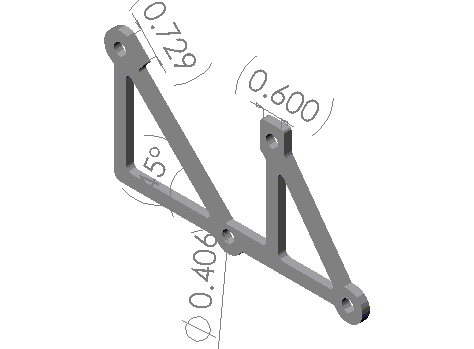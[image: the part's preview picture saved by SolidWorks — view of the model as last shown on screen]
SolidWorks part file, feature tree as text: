
SOLIDWORKS PART (.sldprt)
format: sldprt  version: not decoded by parser v0  size: 442,368 bytes
history: native  units: mm
features: fillet x13, sketch x1, extrude x1 + 1 further entry (+9 scaffold rows collapsed)
feature tree (25):
  "Annotations"  RD1=15.24mm RD2=18.524007mm RD3=45deg RD4=10.3124mm
  scaffold x9  (default folders/planes/origin — collapsed)
  sketch  "Sketch1"  dims[c1.D7=10.3124mm c1.D8=10.3124mm c1.D9=10.3124mm c1.D10=10.3124mm c2.D7=10.3124mm c2.D20=10.3124mm c2.D23=2.54mm c2.D24=2.54mm c2.D25=~12.525847mm c2.D26=~12.460463mm c2.D27=2.54mm c2.D29=7.62mm c2.D30=7.62mm c2.D18=1.27mm c2.D19=2.54mm c2.D31=2.54mm c2.D33=7.62mm c2.D34=1.27mm c2.D35=2.54mm c2.D36=5.08mm c2.D37=2.54mm c2.D38=5.08mm c2.D39=5.08mm c2.D41=7.62mm c2.D14=5.08mm c3.D18=5.08mm c3.D28=5.08mm c3.D30=12.7mm c3.D14=~20.965171mm c4.D28=1.27mm c4.D30=~20.965171mm c4.D18=~13.72589mm c4.D36=10.3124mm c4.D37=10.3124mm c4.D38=10.3124mm c4.D1=25.4mm c4.D2=25.4mm c5.D1=~161.640727mm c6.D1=45.0deg c6.D2=92.075mm c6.D3=~120.52549mm c7.D3=45.0deg c8.D3=92.075mm c8.D4=101.6mm c8.D5=88.9mm c8.D6=~129.320274mm c8.D11=~77.981048mm c9.D11=0.25deg c9.D12=6.35mm c10.D11=~66.14445mm c11.D11=0.0deg c12.D11=6.35mm c12.D12=6.35mm c12.D13=~97.355318mm c13.D13=0.0deg c14.D13=6.35mm c14.D7=6.35mm c14.D9=6.35mm c14.D10=~87.51096mm c15.D10=360.0deg c15.D11=~6.175636mm c16.D10=~86.469108mm c16.D11=~6.175636mm c17.D10=6.35mm c17.D7=6.35mm c17.D9=6.35mm c18.D7=~117.088215mm c19.D7=0.0deg c20.D7=~86.116229mm c21.D7=0.0deg c22.D7=~86.116229mm c23.D7=~0.694885deg c24.D7=~117.088215mm c25.D7=~179.305115deg c26.D7=~117.088215mm c27.D7=0.0deg c28.D7=~130.213714mm c29.D7=0.0deg c30.D7=~64.192579mm c30.D9=~10.081737mm c31.D7=~24.215615mm c32.D7=360.0deg c32.D9=~9.68459mm c33.D7=6.35mm c33.D9=6.35mm c33.D10=6.35mm c33.D11=~89.435083mm c34.D11=0.0deg c35.D11=6.35mm c35.D7=6.35mm c35.D9=~106.448465mm c36.D9=0.0deg c36.D1=~75.270431mm c37.D1=45.0deg c37.D7=~98.145696mm c38.D7=45.0deg c38.D1=~130.213714mm c39.D1=45.0deg c39.D7=6.35mm c39.D9=6.35mm c40.D7=6.35mm c40.D9=5.08mm c40.D10=6.35mm c40.D11=5.08mm c40.D12=~103.685511mm c41.D12=0.0deg c42.D12=5.08mm c42.D13=5.08mm c42.D14=6.35mm c42.D15=6.35mm c42.D16=6.35mm c42.D17=~117.088215mm c43.D17=360.0deg c43.D18=~4.710095mm c44.D17=6.35mm c44.D18=~26.010205mm c45.D18=90.0deg c46.D18=25.4mm c46.D19=25.4mm c46.D20=12.7mm c46.D21=~29.815881mm c47.D21=90.0deg c48.D21=10.16mm c48.D22=10.16mm c48.D23=~103.225696mm c48.D16=~130.213714mm c49.D16=0.0deg c50.D16=5.08mm c50.D27=~17.608588mm c50.D28=12.7mm c50.D29=12.7mm c51.D27=12.7mm c51.D29=~3.480145mm c51.D32=15.24mm c51.D30=~10.642895mm c51.D40=~9.515455mm c51.D14=25.4mm c52.D29=5.08mm c52.D18=12.7mm c52.D28=~25.36823mm c52.D14=12.7mm c53.D28=8.89mm c53.D7=~85.511974mm c54.D7=0.0deg c55.D7=5.08mm c55.D17=5.08mm c55.D24=5.08mm c55.D30=~15.765763mm c55.D15=6.35mm c56.D30=~15.765763mm c56.D15=6.35mm c57.D30=6.35mm c57.D10=5.08mm c57.D15=5.08mm c58.D30=~62.63921mm c58.D34=~60.298777mm c59.D30=~7.405309mm c59.D35=~10.765881mm c59.D36=~122.671739mm c59.D39=16.51mm c60.D30=~7.184205mm c60.D35=~14.803033mm c60.D14=~87.233728deg c60.D36=~176.631101deg]
  extrude  "Extrude6"  Depth=6.35mm
  fillet  "Fillet2"  Radius=5.08mm
  fillet  "Fillet3"  Radius=5.08mm
  fillet  "Fillet4"  Radius=5.08mm
  fillet  "Fillet5"  Radius=2.54mm
  fillet  "Fillet6"  Radius=2.54mm
  fillet  "Fillet9"  Radius=2.54mm
  fillet  "Fillet10"  Radius=1.27mm
  fillet  "Fillet12"  Radius=5.08mm
  fillet  "Fillet13"  Radius=2.54mm
  fillet  "Fillet14"  Radius=2.54mm
  fillet  "Fillet15"  Radius=2.54mm
  fillet  "Fillet16"  Radius=2.54mm
  fillet  "Fillet17"  Radius=2.54mm
decode coverage: 15 of 15 modeling features carry decoded parameters; 1 rows unclassified (native names shown)
note: ~ marks probable driven/reference dimensions
note: suppression state not decoded; provenance and decode notes live in map.json
